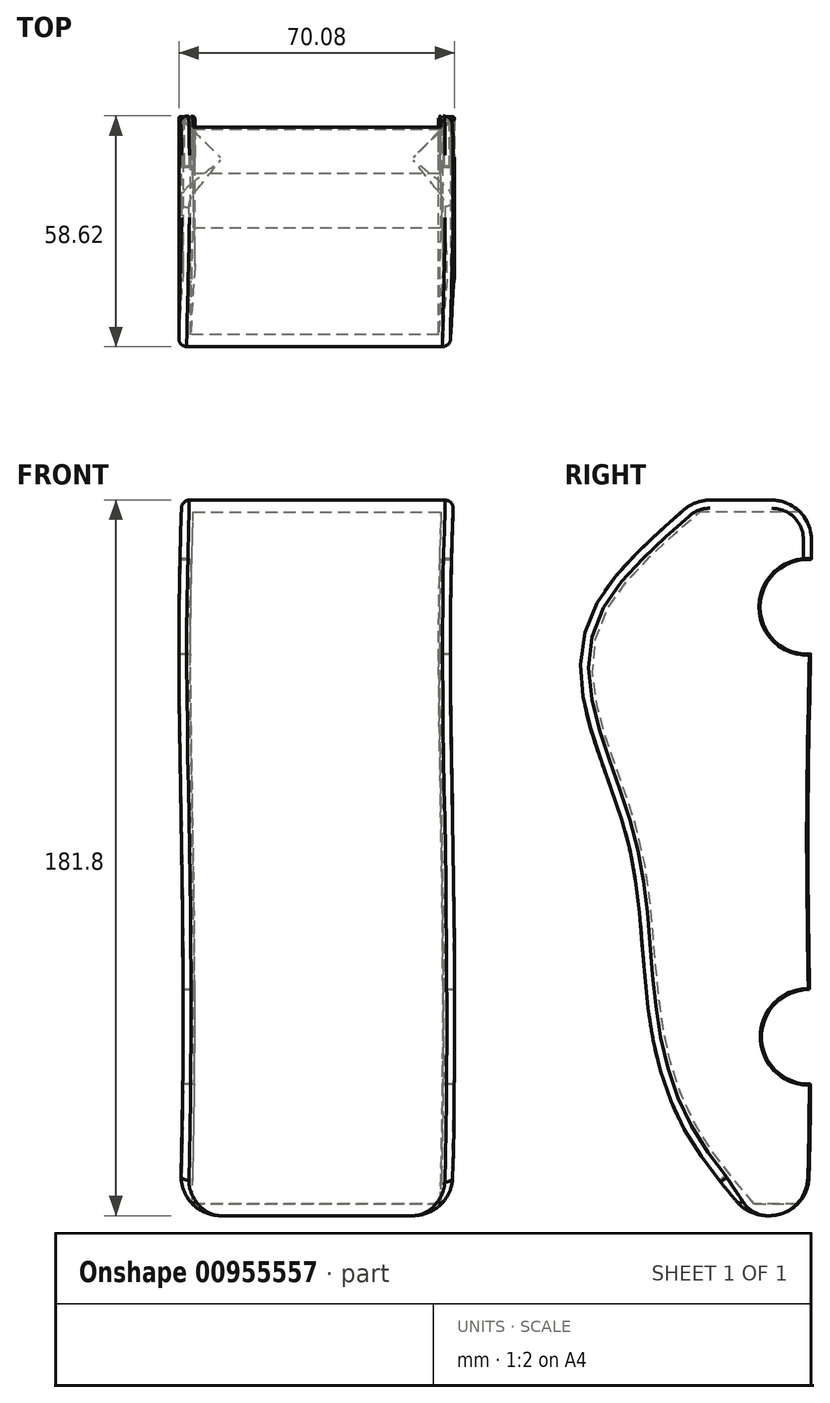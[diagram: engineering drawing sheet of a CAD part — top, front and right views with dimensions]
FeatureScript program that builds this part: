
annotation { "Feature Type Name" : "Feature", "Feature Type Description" : "" }
export const myFeature = defineFeature(function(context is Context, id is Id, definition is map)
    precondition{}
    {
        {
            var Q0;
            Q0=qCreatedBy(makeId("Top.planeOp"),FACE);
            var sketch = newSketch(context, id + "F0", { "sketchPlane" : qUnion([Q0])});
            skLineSegment(sketch, "E0.bottom", {"start": v(34.5, -14.38) * mm, "end": v(-34.5, -14.38) * mm});
            skLineSegment(sketch, "E0.top", {"start": v(34.5, 14.38) * mm, "end": v(-34.5, 14.38) * mm});
            skLineSegment(sketch, "E0.left", {"start": v(34.5, -14.38) * mm, "end": v(34.5, 14.38) * mm});
            skLineSegment(sketch, "E0.right", {"start": v(-34.5, -14.38) * mm, "end": v(-34.5, 14.38) * mm});
            skPoint(sketch, "E0.middle", {"position": v(0, 0) * mm});
            skSolve(sketch);
        }
        {
            var Q0;
            Q0=qCreatedBy(makeId("Top.planeOp"),FACE);
            cPlane(context, id + "F1", {"entities" : qUnion([Q0]), "cplaneType" : CPlaneType.OFFSET, "offset" : 80 * mm, "width" : 150 * mm, "height" : 150 * mm});
        }
        {
            var Q0;
            Q0=qCreatedBy(id+"F1.planeOp",FACE);
            var sketch = newSketch(context, id + "F2", { "sketchPlane" : qUnion([Q0])});
            skLineSegment(sketch, "E1.bottom", {"start": v(-34.6, 13.88) * mm, "end": v(34.4, 13.88) * mm});
            skLineSegment(sketch, "E1.top", {"start": v(-34.6, -32.29) * mm, "end": v(34.4, -32.29) * mm});
            skLineSegment(sketch, "E1.left", {"start": v(-34.6, 13.88) * mm, "end": v(-34.6, -32.29) * mm});
            skLineSegment(sketch, "E1.right", {"start": v(34.4, 13.88) * mm, "end": v(34.4, -32.29) * mm});
            skSolve(sketch);
        }
        {
            var Q0;
            Q0=qCreatedBy(id+"F1.planeOp",FACE);
            cPlane(context, id + "F3", {"entities" : qUnion([Q0]), "cplaneType" : CPlaneType.OFFSET, "offset" : 60 * mm, "width" : 150 * mm, "height" : 150 * mm});
        }
        {
            var Q0;
            Q0=qCreatedBy(id+"F3.planeOp",FACE);
            var sketch = newSketch(context, id + "F4", { "sketchPlane" : qUnion([Q0])});
            skLineSegment(sketch, "E2.bottom", {"start": v(-35.14, 14.76) * mm, "end": v(33.86, 14.76) * mm});
            skLineSegment(sketch, "E2.top", {"start": v(-35.14, -39) * mm, "end": v(33.86, -39) * mm});
            skLineSegment(sketch, "E2.left", {"start": v(-35.14, 14.76) * mm, "end": v(-35.14, -39) * mm});
            skLineSegment(sketch, "E2.right", {"start": v(33.86, 14.76) * mm, "end": v(33.86, -39) * mm});
            skSolve(sketch);
        }
        {
            var Q0;
            Q0=makeQuery(id+"F4.imprint","IMPRINT",FACE,{"disambiguationData":[TD([[makeQuery(id+"F4.imprint","IMPRINT",EDGE,{"derivedFrom":sQuery(id+"F4.wireOp",EDGE,"E2.bottom")}),-1.0]])]});
            cPlane(context, id + "F5", {"entities" : qUnion([Q0]), "cplaneType" : CPlaneType.OFFSET, "offset" : 25 * mm, "width" : 150 * mm, "height" : 150 * mm});
        }
        {
            var Q0;
            Q0=qCreatedBy(id+"F5.planeOp",FACE);
            var sketch = newSketch(context, id + "F6", { "sketchPlane" : qUnion([Q0])});
            skLineSegment(sketch, "E3.bottom", {"start": v(-34.5, -14.73) * mm, "end": v(34.5, -14.73) * mm});
            skLineSegment(sketch, "E3.top", {"start": v(-34.5, 14.73) * mm, "end": v(34.5, 14.73) * mm});
            skLineSegment(sketch, "E3.left", {"start": v(-34.5, -14.73) * mm, "end": v(-34.5, 14.73) * mm});
            skLineSegment(sketch, "E3.right", {"start": v(34.5, -14.73) * mm, "end": v(34.5, 14.73) * mm});
            skPoint(sketch, "E3.middle", {"position": v(0, 0) * mm});
            skSolve(sketch);
        }
        {
            var Q0;
            Q0=qCreatedBy(makeId("Right.planeOp"),FACE);
            var sketch = newSketch(context, id + "F7", { "sketchPlane" : qUnion([Q0])});
            skCircle(sketch, "E4", {"center": v(13.75, 137.88) * mm, "radius": 12 * mm});
            skCircle(sketch, "E5", {"center": v(14.12, 28.64) * mm, "radius": 12 * mm});
            skSolve(sketch);
        }
        {
            var Q0;
            Q0=makeQuery(id+"F0.imprint","IMPRINT",FACE,{"disambiguationData":[TD([[makeQuery(id+"F0.imprint","IMPRINT",EDGE,{"derivedFrom":sQuery(id+"F0.wireOp",EDGE,"E0.bottom")}),-1.0]])]});
            cPlane(context, id + "F8", {"entities" : qUnion([Q0]), "cplaneType" : CPlaneType.OFFSET, "offset" : 16.8 * mm, "oppositeDirection" : true, "width" : 150 * mm, "height" : 150 * mm});
        }
        {
            var Q0;
            Q0=qCreatedBy(id+"F8.planeOp",FACE);
            var sketch = newSketch(context, id + "F9", { "sketchPlane" : qUnion([Q0])});
            skLineSegment(sketch, "E6.bottom", {"start": v(-34.94, -1.1) * mm, "end": v(34.06, -1.1) * mm});
            skLineSegment(sketch, "E6.top", {"start": v(-34.94, 13.85) * mm, "end": v(34.06, 13.85) * mm});
            skLineSegment(sketch, "E6.left", {"start": v(-34.94, -1.1) * mm, "end": v(-34.94, 13.85) * mm});
            skLineSegment(sketch, "E6.right", {"start": v(34.06, -1.1) * mm, "end": v(34.06, 13.85) * mm});
            skSolve(sketch);
        }
        {
            var Q0;
            Q0=makeQuery(id+"F9.imprint","IMPRINT",FACE,{"disambiguationData":[TD([[makeQuery(id+"F9.imprint","IMPRINT",EDGE,{"derivedFrom":sQuery(id+"F9.wireOp",EDGE,"E6.bottom")}),1.0]])]});
            var Q1;
            Q1=makeQuery(id+"F0.imprint","IMPRINT",FACE,{"disambiguationData":[TD([[makeQuery(id+"F0.imprint","IMPRINT",EDGE,{"derivedFrom":sQuery(id+"F0.wireOp",EDGE,"E0.bottom")}),-1.0]])]});
            var Q2;
            Q2=makeQuery(id+"F2.imprint","IMPRINT",FACE,{"disambiguationData":[TD([[makeQuery(id+"F2.imprint","IMPRINT",EDGE,{"derivedFrom":sQuery(id+"F2.wireOp",EDGE,"E1.bottom")}),-1.0]])]});
            var Q3;
            Q3=makeQuery(id+"F4.imprint","IMPRINT",FACE,{"disambiguationData":[TD([[makeQuery(id+"F4.imprint","IMPRINT",EDGE,{"derivedFrom":sQuery(id+"F4.wireOp",EDGE,"E2.bottom")}),-1.0]])]});
            var Q4;
            Q4=makeQuery(id+"F6.imprint","IMPRINT",FACE,{"disambiguationData":[TD([[makeQuery(id+"F6.imprint","IMPRINT",EDGE,{"derivedFrom":sQuery(id+"F6.wireOp",EDGE,"E3.bottom")}),1.0]])]});
            loft(context, id + "F10", {"sheetProfilesArray" : [{ "sheetProfileEntities" : qUnion([Q0]) }, { "sheetProfileEntities" : qUnion([Q1]) }, { "sheetProfileEntities" : qUnion([Q2]) }, { "sheetProfileEntities" : qUnion([Q3]) }, { "sheetProfileEntities" : qUnion([Q4]) }]});
        }
        {
            var Q0;
            Q0=makeQuery(id+"F10.opLoft","SWEPT_FACE",FACE,{"disambiguationData":[OSD([sQuery(id+"F0.wireOp",EDGE,"E0.top"),sQuery(id+"F0.wireOp",EDGE,"E0.left"),sQuery(id+"F0.wireOp",EDGE,"E0.right"),sQuery(id+"F2.wireOp",EDGE,"E1.bottom"),sQuery(id+"F2.wireOp",EDGE,"E1.left"),sQuery(id+"F2.wireOp",EDGE,"E1.right"),sQuery(id+"F4.wireOp",EDGE,"E2.bottom"),sQuery(id+"F4.wireOp",EDGE,"E2.left"),sQuery(id+"F4.wireOp",EDGE,"E2.right"),sQuery(id+"F6.wireOp",EDGE,"E3.top"),sQuery(id+"F6.wireOp",EDGE,"E3.left"),sQuery(id+"F6.wireOp",EDGE,"E3.right"),sQuery(id+"F9.wireOp",EDGE,"E6.top"),sQuery(id+"F9.wireOp",EDGE,"E6.left"),sQuery(id+"F9.wireOp",EDGE,"E6.right")])]});
            shell(context, id + "F11", {"entities" : qUnion([Q0]), "thickness" : 3 * mm});
        }
        {
            var Q0;
            Q0=makeQuery(id+"F7.imprint","IMPRINT",FACE,{"disambiguationData":[TD([[makeQuery(id+"F7.imprint","IMPRINT",EDGE,{"derivedFrom":sQuery(id+"F7.wireOp",EDGE,"E5")}),1.0]])]});
            var Q1;
            Q1=makeQuery(id+"F7.imprint","IMPRINT",FACE,{"disambiguationData":[TD([[makeQuery(id+"F7.imprint","IMPRINT",EDGE,{"derivedFrom":sQuery(id+"F7.wireOp",EDGE,"E4")}),1.0]])]});
            extrude(context, id + "F12", {"entities" : qUnion([Q0, Q1]), "operationType" : NewBodyOperationType.REMOVE, "endBound" : BoundingType.SYMMETRIC, "oppositeDirection" : true, "depth" : 5000 * mm, "offsetDistance" : 25 * mm});
        }
        {
            var Q0;
            Q0=makeQuery(id+"F10.opLoft","CAP_FACE",FACE,{"disambiguationData":[OSD([makeQuery(id+"F9.imprint","IMPRINT",FACE,{"disambiguationData":[TD([[makeQuery(id+"F9.imprint","IMPRINT",EDGE,{"derivedFrom":sQuery(id+"F9.wireOp",EDGE,"E6.bottom")}),1.0]])]})])],"isStart":true});
            fillet(context, id + "F13", {"entities" : qUnion([Q0]), "radius" : 10 * mm, "tangentPropagation" : true, "allowEdgeOverflow" : false});
        }
        {
            var Q0;
            Q0=makeQuery(id+"F10.opLoft","MID_CAP_EDGE",EDGE,{"disambiguationData":[OSD([sQuery(id+"F6.wireOp",EDGE,"E3.top"),sQuery(id+"F6.wireOp",EDGE,"E3.left"),sQuery(id+"F6.wireOp",EDGE,"E3.right")])],"capPos":4.0});
            fillet(context, id + "F14", {"entities" : qUnion([Q0]), "radius" : 10 * mm, "tangentPropagation" : true, "allowEdgeOverflow" : false});
        }
        {
            var Q0;
            Q0=makeQuery(id+"F10.opLoft","MID_CAP_EDGE",EDGE,{"disambiguationData":[OSD([sQuery(id+"F6.wireOp",EDGE,"E3.bottom"),sQuery(id+"F6.wireOp",EDGE,"E3.left"),sQuery(id+"F6.wireOp",EDGE,"E3.right")])],"capPos":4.0});
            fillet(context, id + "F15", {"entities" : qUnion([Q0]), "radius" : 10 * mm, "tangentPropagation" : true, "allowEdgeOverflow" : false});
        }
        {
            var Q0;
            Q0=makeQuery(id+"F10.opLoft","SWEPT_EDGE",EDGE,{"disambiguationData":[OSD([sQuery(id+"F0.wireOp",EDGE,"E0.bottom"),sQuery(id+"F0.wireOp",EDGE,"E0.right"),sQuery(id+"F2.wireOp",EDGE,"E1.top"),sQuery(id+"F2.wireOp",EDGE,"E1.left"),sQuery(id+"F4.wireOp",EDGE,"E2.top"),sQuery(id+"F4.wireOp",EDGE,"E2.left"),sQuery(id+"F6.wireOp",EDGE,"E3.bottom"),sQuery(id+"F6.wireOp",EDGE,"E3.left"),sQuery(id+"F9.wireOp",EDGE,"E6.bottom"),sQuery(id+"F9.wireOp",EDGE,"E6.left")])]});
            var Q1;
            Q1=makeQuery(id+"F10.opLoft","SWEPT_EDGE",EDGE,{"disambiguationData":[OSD([sQuery(id+"F0.wireOp",EDGE,"E0.bottom"),sQuery(id+"F0.wireOp",EDGE,"E0.left"),sQuery(id+"F2.wireOp",EDGE,"E1.top"),sQuery(id+"F2.wireOp",EDGE,"E1.right"),sQuery(id+"F4.wireOp",EDGE,"E2.top"),sQuery(id+"F4.wireOp",EDGE,"E2.right"),sQuery(id+"F6.wireOp",EDGE,"E3.bottom"),sQuery(id+"F6.wireOp",EDGE,"E3.right"),sQuery(id+"F9.wireOp",EDGE,"E6.bottom"),sQuery(id+"F9.wireOp",EDGE,"E6.right")])]});
            fillet(context, id + "F16", {"entities" : qUnion([Q0, Q1]), "radius" : 2 * mm, "tangentPropagation" : true, "allowEdgeOverflow" : false});
        }
        {
            var Q0;
            {var subQ0=sQuery(id+"F9.wireOp",EDGE,"E6.left");var subQ1=sQuery(id+"F9.wireOp",EDGE,"E6.top");var subQ2=sQuery(id+"F6.wireOp",EDGE,"E3.left");var subQ3=sQuery(id+"F6.wireOp",EDGE,"E3.top");var subQ4=sQuery(id+"F4.wireOp",EDGE,"E2.left");var subQ5=sQuery(id+"F4.wireOp",EDGE,"E2.bottom");var subQ6=sQuery(id+"F2.wireOp",EDGE,"E1.left");var subQ7=sQuery(id+"F2.wireOp",EDGE,"E1.bottom");var subQ8=sQuery(id+"F0.wireOp",EDGE,"E0.right");var subQ9=sQuery(id+"F0.wireOp",EDGE,"E0.top");Q0=makeQuery(id+"F12.boolean.opBoolean","SPLIT",EDGE,{"disambiguationData":[TD([makeQuery(id+"F10.opLoft","SWEPT_FACE",FACE,{"disambiguationData":[OSD([sQuery(id+"F0.wireOp",EDGE,"E0.bottom"),subQ9,subQ8,subQ7,sQuery(id+"F2.wireOp",EDGE,"E1.top"),subQ6,subQ5,sQuery(id+"F4.wireOp",EDGE,"E2.top"),subQ4,sQuery(id+"F6.wireOp",EDGE,"E3.bottom"),subQ3,subQ2,sQuery(id+"F9.wireOp",EDGE,"E6.bottom"),subQ1,subQ0])]}),makeQuery(id+"F10.opLoft","SWEPT_FACE",FACE,{"disambiguationData":[OSD([subQ9,sQuery(id+"F0.wireOp",EDGE,"E0.left"),subQ8,subQ7,subQ6,sQuery(id+"F2.wireOp",EDGE,"E1.right"),subQ5,subQ4,sQuery(id+"F4.wireOp",EDGE,"E2.right"),subQ3,subQ2,sQuery(id+"F6.wireOp",EDGE,"E3.right"),subQ1,subQ0,sQuery(id+"F9.wireOp",EDGE,"E6.right")])]}),makeQuery(id+"F12.opExtrude","SWEPT_FACE",FACE,{"disambiguationData":[OSD([sQuery(id+"F7.wireOp",EDGE,"E4")])]}),makeQuery(id+"F12.opExtrude","SWEPT_FACE",FACE,{"disambiguationData":[OSD([sQuery(id+"F7.wireOp",EDGE,"E5")])]})])],"derivedFrom":makeQuery(id+"F10.opLoft","SWEPT_EDGE",EDGE,{"disambiguationData":[OSD([subQ9,subQ8,subQ7,subQ6,subQ5,subQ4,subQ3,subQ2,subQ1,subQ0])]})});}
            var Q1;
            Q1=makeQuery(id+"F12.boolean.opBoolean","INTERSECT",EDGE,{"derivedFrom":[makeQuery(id+"F10.opLoft","SWEPT_FACE",FACE,{"disambiguationData":[OSD([sQuery(id+"F0.wireOp",EDGE,"E0.bottom"),sQuery(id+"F0.wireOp",EDGE,"E0.top"),sQuery(id+"F0.wireOp",EDGE,"E0.right"),sQuery(id+"F2.wireOp",EDGE,"E1.bottom"),sQuery(id+"F2.wireOp",EDGE,"E1.top"),sQuery(id+"F2.wireOp",EDGE,"E1.left"),sQuery(id+"F4.wireOp",EDGE,"E2.bottom"),sQuery(id+"F4.wireOp",EDGE,"E2.top"),sQuery(id+"F4.wireOp",EDGE,"E2.left"),sQuery(id+"F6.wireOp",EDGE,"E3.bottom"),sQuery(id+"F6.wireOp",EDGE,"E3.top"),sQuery(id+"F6.wireOp",EDGE,"E3.left"),sQuery(id+"F9.wireOp",EDGE,"E6.bottom"),sQuery(id+"F9.wireOp",EDGE,"E6.top"),sQuery(id+"F9.wireOp",EDGE,"E6.left")])]}),makeQuery(id+"F12.opExtrude","SWEPT_FACE",FACE,{"disambiguationData":[OSD([sQuery(id+"F7.wireOp",EDGE,"E4")])]})]});
            var Q2;
            {var subQ0=sQuery(id+"F9.wireOp",EDGE,"E6.left");var subQ1=sQuery(id+"F9.wireOp",EDGE,"E6.top");var subQ2=sQuery(id+"F9.wireOp",EDGE,"E6.bottom");var subQ3=sQuery(id+"F6.wireOp",EDGE,"E3.left");var subQ4=sQuery(id+"F6.wireOp",EDGE,"E3.top");var subQ5=sQuery(id+"F4.wireOp",EDGE,"E2.left");var subQ6=sQuery(id+"F4.wireOp",EDGE,"E2.bottom");var subQ7=sQuery(id+"F2.wireOp",EDGE,"E1.left");var subQ8=sQuery(id+"F2.wireOp",EDGE,"E1.bottom");var subQ9=sQuery(id+"F0.wireOp",EDGE,"E0.right");var subQ10=sQuery(id+"F0.wireOp",EDGE,"E0.top");var subQ11=sQuery(id+"F9.wireOp",EDGE,"E6.right");Q2=makeQuery(id+"F12.boolean.opBoolean","SPLIT",EDGE,{"disambiguationData":[TD([makeQuery(id+"F10.opLoft","SWEPT_FACE",FACE,{"disambiguationData":[OSD([sQuery(id+"F0.wireOp",EDGE,"E0.bottom"),subQ10,subQ9,subQ8,sQuery(id+"F2.wireOp",EDGE,"E1.top"),subQ7,subQ6,sQuery(id+"F4.wireOp",EDGE,"E2.top"),subQ5,sQuery(id+"F6.wireOp",EDGE,"E3.bottom"),subQ4,subQ3,subQ2,subQ1,subQ0])]}),makeQuery(id+"F10.opLoft","SWEPT_FACE",FACE,{"disambiguationData":[OSD([subQ10,sQuery(id+"F0.wireOp",EDGE,"E0.left"),subQ9,subQ8,subQ7,sQuery(id+"F2.wireOp",EDGE,"E1.right"),subQ6,subQ5,sQuery(id+"F4.wireOp",EDGE,"E2.right"),subQ4,subQ3,sQuery(id+"F6.wireOp",EDGE,"E3.right"),subQ1,subQ0,subQ11])]}),makeQuery(id+"F10.opLoft","CAP_FACE",FACE,{"disambiguationData":[OSD([makeQuery(id+"F9.imprint","IMPRINT",FACE,{"disambiguationData":[TD([[makeQuery(id+"F9.imprint","IMPRINT",EDGE,{"derivedFrom":subQ2}),1.0]])]})])],"isStart":true}),makeQuery(id+"F12.opExtrude","SWEPT_FACE",FACE,{"disambiguationData":[OSD([sQuery(id+"F7.wireOp",EDGE,"E5")])]})])],"derivedFrom":makeQuery(id+"F10.opLoft","SWEPT_EDGE",EDGE,{"disambiguationData":[OSD([subQ10,subQ9,subQ8,subQ7,subQ6,subQ5,subQ4,subQ3,subQ1,subQ0])]})});}
            var Q3;
            Q3=makeQuery(id+"F12.boolean.opBoolean","INTERSECT",EDGE,{"derivedFrom":[makeQuery(id+"F10.opLoft","SWEPT_FACE",FACE,{"disambiguationData":[OSD([sQuery(id+"F0.wireOp",EDGE,"E0.bottom"),sQuery(id+"F0.wireOp",EDGE,"E0.top"),sQuery(id+"F0.wireOp",EDGE,"E0.right"),sQuery(id+"F2.wireOp",EDGE,"E1.bottom"),sQuery(id+"F2.wireOp",EDGE,"E1.top"),sQuery(id+"F2.wireOp",EDGE,"E1.left"),sQuery(id+"F4.wireOp",EDGE,"E2.bottom"),sQuery(id+"F4.wireOp",EDGE,"E2.top"),sQuery(id+"F4.wireOp",EDGE,"E2.left"),sQuery(id+"F6.wireOp",EDGE,"E3.bottom"),sQuery(id+"F6.wireOp",EDGE,"E3.top"),sQuery(id+"F6.wireOp",EDGE,"E3.left"),sQuery(id+"F9.wireOp",EDGE,"E6.bottom"),sQuery(id+"F9.wireOp",EDGE,"E6.top"),sQuery(id+"F9.wireOp",EDGE,"E6.left")])]}),makeQuery(id+"F12.opExtrude","SWEPT_FACE",FACE,{"disambiguationData":[OSD([sQuery(id+"F7.wireOp",EDGE,"E5")])]})]});
            var Q4;
            Q4=makeQuery(id+"F12.boolean.opBoolean","INTERSECT",EDGE,{"derivedFrom":[makeQuery(id+"F11.opShell","OFFSET_FACE",FACE,{"disambiguationData":[OSD([sQuery(id+"F0.wireOp",EDGE,"E0.bottom"),sQuery(id+"F0.wireOp",EDGE,"E0.top"),sQuery(id+"F0.wireOp",EDGE,"E0.right"),sQuery(id+"F2.wireOp",EDGE,"E1.bottom"),sQuery(id+"F2.wireOp",EDGE,"E1.top"),sQuery(id+"F2.wireOp",EDGE,"E1.left"),sQuery(id+"F4.wireOp",EDGE,"E2.bottom"),sQuery(id+"F4.wireOp",EDGE,"E2.top"),sQuery(id+"F4.wireOp",EDGE,"E2.left"),sQuery(id+"F6.wireOp",EDGE,"E3.bottom"),sQuery(id+"F6.wireOp",EDGE,"E3.top"),sQuery(id+"F6.wireOp",EDGE,"E3.left"),sQuery(id+"F9.wireOp",EDGE,"E6.bottom"),sQuery(id+"F9.wireOp",EDGE,"E6.top"),sQuery(id+"F9.wireOp",EDGE,"E6.left")])]}),makeQuery(id+"F12.opExtrude","SWEPT_FACE",FACE,{"disambiguationData":[OSD([sQuery(id+"F7.wireOp",EDGE,"E5")])]})]});
            var Q5;
            {var subQ0=sQuery(id+"F9.wireOp",EDGE,"E6.left");var subQ1=sQuery(id+"F9.wireOp",EDGE,"E6.top");var subQ2=sQuery(id+"F6.wireOp",EDGE,"E3.left");var subQ3=sQuery(id+"F6.wireOp",EDGE,"E3.top");var subQ4=sQuery(id+"F4.wireOp",EDGE,"E2.left");var subQ5=sQuery(id+"F4.wireOp",EDGE,"E2.bottom");var subQ6=sQuery(id+"F2.wireOp",EDGE,"E1.left");var subQ7=sQuery(id+"F2.wireOp",EDGE,"E1.bottom");var subQ8=sQuery(id+"F0.wireOp",EDGE,"E0.right");var subQ9=sQuery(id+"F0.wireOp",EDGE,"E0.top");Q5=makeQuery(id+"F12.boolean.opBoolean","SPLIT",EDGE,{"disambiguationData":[TD([makeQuery(id+"F10.opLoft","SWEPT_FACE",FACE,{"disambiguationData":[OSD([subQ9,sQuery(id+"F0.wireOp",EDGE,"E0.left"),subQ8,subQ7,subQ6,sQuery(id+"F2.wireOp",EDGE,"E1.right"),subQ5,subQ4,sQuery(id+"F4.wireOp",EDGE,"E2.right"),subQ3,subQ2,sQuery(id+"F6.wireOp",EDGE,"E3.right"),subQ1,subQ0,sQuery(id+"F9.wireOp",EDGE,"E6.right")])]}),makeQuery(id+"F11.opShell","OFFSET_FACE",FACE,{"disambiguationData":[OSD([sQuery(id+"F0.wireOp",EDGE,"E0.bottom"),subQ9,subQ8,subQ7,sQuery(id+"F2.wireOp",EDGE,"E1.top"),subQ6,subQ5,sQuery(id+"F4.wireOp",EDGE,"E2.top"),subQ4,sQuery(id+"F6.wireOp",EDGE,"E3.bottom"),subQ3,subQ2,sQuery(id+"F9.wireOp",EDGE,"E6.bottom"),subQ1,subQ0])]}),makeQuery(id+"F12.opExtrude","SWEPT_FACE",FACE,{"disambiguationData":[OSD([sQuery(id+"F7.wireOp",EDGE,"E4")])]}),makeQuery(id+"F12.opExtrude","SWEPT_FACE",FACE,{"disambiguationData":[OSD([sQuery(id+"F7.wireOp",EDGE,"E5")])]})])],"derivedFrom":makeQuery(id+"F11.opShell","OFFSET_EDGE",EDGE,{"disambiguationData":[OSD([subQ9,subQ8,subQ7,subQ6,subQ5,subQ4,subQ3,subQ2,subQ1,subQ0])]})});}
            var Q6;
            Q6=makeQuery(id+"F12.boolean.opBoolean","INTERSECT",EDGE,{"derivedFrom":[makeQuery(id+"F11.opShell","OFFSET_FACE",FACE,{"disambiguationData":[OSD([sQuery(id+"F0.wireOp",EDGE,"E0.bottom"),sQuery(id+"F0.wireOp",EDGE,"E0.top"),sQuery(id+"F0.wireOp",EDGE,"E0.right"),sQuery(id+"F2.wireOp",EDGE,"E1.bottom"),sQuery(id+"F2.wireOp",EDGE,"E1.top"),sQuery(id+"F2.wireOp",EDGE,"E1.left"),sQuery(id+"F4.wireOp",EDGE,"E2.bottom"),sQuery(id+"F4.wireOp",EDGE,"E2.top"),sQuery(id+"F4.wireOp",EDGE,"E2.left"),sQuery(id+"F6.wireOp",EDGE,"E3.bottom"),sQuery(id+"F6.wireOp",EDGE,"E3.top"),sQuery(id+"F6.wireOp",EDGE,"E3.left"),sQuery(id+"F9.wireOp",EDGE,"E6.bottom"),sQuery(id+"F9.wireOp",EDGE,"E6.top"),sQuery(id+"F9.wireOp",EDGE,"E6.left")])]}),makeQuery(id+"F12.opExtrude","SWEPT_FACE",FACE,{"disambiguationData":[OSD([sQuery(id+"F7.wireOp",EDGE,"E4")])]})]});
            var Q7;
            {var subQ0=sQuery(id+"F9.wireOp",EDGE,"E6.right");var subQ1=sQuery(id+"F9.wireOp",EDGE,"E6.top");var subQ2=sQuery(id+"F6.wireOp",EDGE,"E3.right");var subQ3=sQuery(id+"F6.wireOp",EDGE,"E3.top");var subQ4=sQuery(id+"F4.wireOp",EDGE,"E2.right");var subQ5=sQuery(id+"F4.wireOp",EDGE,"E2.bottom");var subQ6=sQuery(id+"F2.wireOp",EDGE,"E1.right");var subQ7=sQuery(id+"F2.wireOp",EDGE,"E1.bottom");var subQ8=sQuery(id+"F0.wireOp",EDGE,"E0.left");var subQ9=sQuery(id+"F0.wireOp",EDGE,"E0.top");Q7=makeQuery(id+"F12.boolean.opBoolean","SPLIT",EDGE,{"disambiguationData":[TD([makeQuery(id+"F10.opLoft","SWEPT_FACE",FACE,{"disambiguationData":[OSD([sQuery(id+"F0.wireOp",EDGE,"E0.bottom"),subQ9,subQ8,subQ7,sQuery(id+"F2.wireOp",EDGE,"E1.top"),subQ6,subQ5,sQuery(id+"F4.wireOp",EDGE,"E2.top"),subQ4,sQuery(id+"F6.wireOp",EDGE,"E3.bottom"),subQ3,subQ2,sQuery(id+"F9.wireOp",EDGE,"E6.bottom"),subQ1,subQ0])]}),makeQuery(id+"F10.opLoft","SWEPT_FACE",FACE,{"disambiguationData":[OSD([subQ9,subQ8,sQuery(id+"F0.wireOp",EDGE,"E0.right"),subQ7,sQuery(id+"F2.wireOp",EDGE,"E1.left"),subQ6,subQ5,sQuery(id+"F4.wireOp",EDGE,"E2.left"),subQ4,subQ3,sQuery(id+"F6.wireOp",EDGE,"E3.left"),subQ2,subQ1,sQuery(id+"F9.wireOp",EDGE,"E6.left"),subQ0])]}),makeQuery(id+"F12.opExtrude","SWEPT_FACE",FACE,{"disambiguationData":[OSD([sQuery(id+"F7.wireOp",EDGE,"E4")])]}),makeQuery(id+"F12.opExtrude","SWEPT_FACE",FACE,{"disambiguationData":[OSD([sQuery(id+"F7.wireOp",EDGE,"E5")])]})])],"derivedFrom":makeQuery(id+"F10.opLoft","SWEPT_EDGE",EDGE,{"disambiguationData":[OSD([subQ9,subQ8,subQ7,subQ6,subQ5,subQ4,subQ3,subQ2,subQ1,subQ0])]})});}
            var Q8;
            {var subQ0=sQuery(id+"F9.wireOp",EDGE,"E6.right");var subQ1=sQuery(id+"F9.wireOp",EDGE,"E6.top");var subQ2=sQuery(id+"F6.wireOp",EDGE,"E3.right");var subQ3=sQuery(id+"F6.wireOp",EDGE,"E3.top");var subQ4=sQuery(id+"F4.wireOp",EDGE,"E2.right");var subQ5=sQuery(id+"F4.wireOp",EDGE,"E2.bottom");var subQ6=sQuery(id+"F2.wireOp",EDGE,"E1.right");var subQ7=sQuery(id+"F2.wireOp",EDGE,"E1.bottom");var subQ8=sQuery(id+"F0.wireOp",EDGE,"E0.left");var subQ9=sQuery(id+"F0.wireOp",EDGE,"E0.top");Q8=makeQuery(id+"F12.boolean.opBoolean","SPLIT",EDGE,{"disambiguationData":[TD([makeQuery(id+"F10.opLoft","SWEPT_FACE",FACE,{"disambiguationData":[OSD([subQ9,subQ8,sQuery(id+"F0.wireOp",EDGE,"E0.right"),subQ7,sQuery(id+"F2.wireOp",EDGE,"E1.left"),subQ6,subQ5,sQuery(id+"F4.wireOp",EDGE,"E2.left"),subQ4,subQ3,sQuery(id+"F6.wireOp",EDGE,"E3.left"),subQ2,subQ1,sQuery(id+"F9.wireOp",EDGE,"E6.left"),subQ0])]}),makeQuery(id+"F11.opShell","OFFSET_FACE",FACE,{"disambiguationData":[OSD([sQuery(id+"F0.wireOp",EDGE,"E0.bottom"),subQ9,subQ8,subQ7,sQuery(id+"F2.wireOp",EDGE,"E1.top"),subQ6,subQ5,sQuery(id+"F4.wireOp",EDGE,"E2.top"),subQ4,sQuery(id+"F6.wireOp",EDGE,"E3.bottom"),subQ3,subQ2,sQuery(id+"F9.wireOp",EDGE,"E6.bottom"),subQ1,subQ0])]}),makeQuery(id+"F12.opExtrude","SWEPT_FACE",FACE,{"disambiguationData":[OSD([sQuery(id+"F7.wireOp",EDGE,"E4")])]}),makeQuery(id+"F12.opExtrude","SWEPT_FACE",FACE,{"disambiguationData":[OSD([sQuery(id+"F7.wireOp",EDGE,"E5")])]})])],"derivedFrom":makeQuery(id+"F11.opShell","OFFSET_EDGE",EDGE,{"disambiguationData":[OSD([subQ9,subQ8,subQ7,subQ6,subQ5,subQ4,subQ3,subQ2,subQ1,subQ0])]})});}
            var Q9;
            Q9=makeQuery(id+"F12.boolean.opBoolean","INTERSECT",EDGE,{"derivedFrom":[makeQuery(id+"F10.opLoft","SWEPT_FACE",FACE,{"disambiguationData":[OSD([sQuery(id+"F0.wireOp",EDGE,"E0.bottom"),sQuery(id+"F0.wireOp",EDGE,"E0.top"),sQuery(id+"F0.wireOp",EDGE,"E0.left"),sQuery(id+"F2.wireOp",EDGE,"E1.bottom"),sQuery(id+"F2.wireOp",EDGE,"E1.top"),sQuery(id+"F2.wireOp",EDGE,"E1.right"),sQuery(id+"F4.wireOp",EDGE,"E2.bottom"),sQuery(id+"F4.wireOp",EDGE,"E2.top"),sQuery(id+"F4.wireOp",EDGE,"E2.right"),sQuery(id+"F6.wireOp",EDGE,"E3.bottom"),sQuery(id+"F6.wireOp",EDGE,"E3.top"),sQuery(id+"F6.wireOp",EDGE,"E3.right"),sQuery(id+"F9.wireOp",EDGE,"E6.bottom"),sQuery(id+"F9.wireOp",EDGE,"E6.top"),sQuery(id+"F9.wireOp",EDGE,"E6.right")])]}),makeQuery(id+"F12.opExtrude","SWEPT_FACE",FACE,{"disambiguationData":[OSD([sQuery(id+"F7.wireOp",EDGE,"E4")])]})]});
            var Q10;
            Q10=makeQuery(id+"F12.boolean.opBoolean","INTERSECT",EDGE,{"derivedFrom":[makeQuery(id+"F11.opShell","OFFSET_FACE",FACE,{"disambiguationData":[OSD([sQuery(id+"F0.wireOp",EDGE,"E0.bottom"),sQuery(id+"F0.wireOp",EDGE,"E0.top"),sQuery(id+"F0.wireOp",EDGE,"E0.left"),sQuery(id+"F2.wireOp",EDGE,"E1.bottom"),sQuery(id+"F2.wireOp",EDGE,"E1.top"),sQuery(id+"F2.wireOp",EDGE,"E1.right"),sQuery(id+"F4.wireOp",EDGE,"E2.bottom"),sQuery(id+"F4.wireOp",EDGE,"E2.top"),sQuery(id+"F4.wireOp",EDGE,"E2.right"),sQuery(id+"F6.wireOp",EDGE,"E3.bottom"),sQuery(id+"F6.wireOp",EDGE,"E3.top"),sQuery(id+"F6.wireOp",EDGE,"E3.right"),sQuery(id+"F9.wireOp",EDGE,"E6.bottom"),sQuery(id+"F9.wireOp",EDGE,"E6.top"),sQuery(id+"F9.wireOp",EDGE,"E6.right")])]}),makeQuery(id+"F12.opExtrude","SWEPT_FACE",FACE,{"disambiguationData":[OSD([sQuery(id+"F7.wireOp",EDGE,"E4")])]})]});
            var Q11;
            Q11=makeQuery(id+"F12.boolean.opBoolean","INTERSECT",EDGE,{"derivedFrom":[makeQuery(id+"F10.opLoft","SWEPT_FACE",FACE,{"disambiguationData":[OSD([sQuery(id+"F0.wireOp",EDGE,"E0.bottom"),sQuery(id+"F0.wireOp",EDGE,"E0.top"),sQuery(id+"F0.wireOp",EDGE,"E0.left"),sQuery(id+"F2.wireOp",EDGE,"E1.bottom"),sQuery(id+"F2.wireOp",EDGE,"E1.top"),sQuery(id+"F2.wireOp",EDGE,"E1.right"),sQuery(id+"F4.wireOp",EDGE,"E2.bottom"),sQuery(id+"F4.wireOp",EDGE,"E2.top"),sQuery(id+"F4.wireOp",EDGE,"E2.right"),sQuery(id+"F6.wireOp",EDGE,"E3.bottom"),sQuery(id+"F6.wireOp",EDGE,"E3.top"),sQuery(id+"F6.wireOp",EDGE,"E3.right"),sQuery(id+"F9.wireOp",EDGE,"E6.bottom"),sQuery(id+"F9.wireOp",EDGE,"E6.top"),sQuery(id+"F9.wireOp",EDGE,"E6.right")])]}),makeQuery(id+"F12.opExtrude","SWEPT_FACE",FACE,{"disambiguationData":[OSD([sQuery(id+"F7.wireOp",EDGE,"E5")])]})]});
            var Q12;
            Q12=makeQuery(id+"F12.boolean.opBoolean","INTERSECT",EDGE,{"derivedFrom":[makeQuery(id+"F11.opShell","OFFSET_FACE",FACE,{"disambiguationData":[OSD([sQuery(id+"F0.wireOp",EDGE,"E0.bottom"),sQuery(id+"F0.wireOp",EDGE,"E0.top"),sQuery(id+"F0.wireOp",EDGE,"E0.left"),sQuery(id+"F2.wireOp",EDGE,"E1.bottom"),sQuery(id+"F2.wireOp",EDGE,"E1.top"),sQuery(id+"F2.wireOp",EDGE,"E1.right"),sQuery(id+"F4.wireOp",EDGE,"E2.bottom"),sQuery(id+"F4.wireOp",EDGE,"E2.top"),sQuery(id+"F4.wireOp",EDGE,"E2.right"),sQuery(id+"F6.wireOp",EDGE,"E3.bottom"),sQuery(id+"F6.wireOp",EDGE,"E3.top"),sQuery(id+"F6.wireOp",EDGE,"E3.right"),sQuery(id+"F9.wireOp",EDGE,"E6.bottom"),sQuery(id+"F9.wireOp",EDGE,"E6.top"),sQuery(id+"F9.wireOp",EDGE,"E6.right")])]}),makeQuery(id+"F12.opExtrude","SWEPT_FACE",FACE,{"disambiguationData":[OSD([sQuery(id+"F7.wireOp",EDGE,"E5")])]})]});
            var Q13;
            {var subQ0=sQuery(id+"F9.wireOp",EDGE,"E6.right");var subQ1=sQuery(id+"F9.wireOp",EDGE,"E6.top");var subQ2=sQuery(id+"F9.wireOp",EDGE,"E6.bottom");var subQ3=sQuery(id+"F6.wireOp",EDGE,"E3.right");var subQ4=sQuery(id+"F6.wireOp",EDGE,"E3.top");var subQ5=sQuery(id+"F4.wireOp",EDGE,"E2.right");var subQ6=sQuery(id+"F4.wireOp",EDGE,"E2.bottom");var subQ7=sQuery(id+"F2.wireOp",EDGE,"E1.right");var subQ8=sQuery(id+"F2.wireOp",EDGE,"E1.bottom");var subQ9=sQuery(id+"F0.wireOp",EDGE,"E0.left");var subQ10=sQuery(id+"F0.wireOp",EDGE,"E0.top");var subQ11=sQuery(id+"F9.wireOp",EDGE,"E6.left");Q13=makeQuery(id+"F12.boolean.opBoolean","SPLIT",EDGE,{"disambiguationData":[TD([makeQuery(id+"F10.opLoft","SWEPT_FACE",FACE,{"disambiguationData":[OSD([sQuery(id+"F0.wireOp",EDGE,"E0.bottom"),subQ10,subQ9,subQ8,sQuery(id+"F2.wireOp",EDGE,"E1.top"),subQ7,subQ6,sQuery(id+"F4.wireOp",EDGE,"E2.top"),subQ5,sQuery(id+"F6.wireOp",EDGE,"E3.bottom"),subQ4,subQ3,subQ2,subQ1,subQ0])]}),makeQuery(id+"F10.opLoft","SWEPT_FACE",FACE,{"disambiguationData":[OSD([subQ10,subQ9,sQuery(id+"F0.wireOp",EDGE,"E0.right"),subQ8,sQuery(id+"F2.wireOp",EDGE,"E1.left"),subQ7,subQ6,sQuery(id+"F4.wireOp",EDGE,"E2.left"),subQ5,subQ4,sQuery(id+"F6.wireOp",EDGE,"E3.left"),subQ3,subQ1,subQ11,subQ0])]}),makeQuery(id+"F10.opLoft","CAP_FACE",FACE,{"disambiguationData":[OSD([makeQuery(id+"F9.imprint","IMPRINT",FACE,{"disambiguationData":[TD([[makeQuery(id+"F9.imprint","IMPRINT",EDGE,{"derivedFrom":subQ2}),1.0]])]})])],"isStart":true}),makeQuery(id+"F12.opExtrude","SWEPT_FACE",FACE,{"disambiguationData":[OSD([sQuery(id+"F7.wireOp",EDGE,"E5")])]})])],"derivedFrom":makeQuery(id+"F10.opLoft","SWEPT_EDGE",EDGE,{"disambiguationData":[OSD([subQ10,subQ9,subQ8,subQ7,subQ6,subQ5,subQ4,subQ3,subQ1,subQ0])]})});}
            var Q14;
            {var subQ0=sQuery(id+"F9.wireOp",EDGE,"E6.right");var subQ1=sQuery(id+"F9.wireOp",EDGE,"E6.left");var subQ2=sQuery(id+"F9.wireOp",EDGE,"E6.top");var subQ3=sQuery(id+"F6.wireOp",EDGE,"E3.right");var subQ4=sQuery(id+"F6.wireOp",EDGE,"E3.top");var subQ5=sQuery(id+"F4.wireOp",EDGE,"E2.right");var subQ6=sQuery(id+"F4.wireOp",EDGE,"E2.bottom");var subQ7=sQuery(id+"F2.wireOp",EDGE,"E1.right");var subQ8=sQuery(id+"F2.wireOp",EDGE,"E1.bottom");var subQ9=sQuery(id+"F0.wireOp",EDGE,"E0.left");var subQ10=sQuery(id+"F0.wireOp",EDGE,"E0.top");var subQ11=sQuery(id+"F9.wireOp",EDGE,"E6.bottom");Q14=makeQuery(id+"F12.boolean.opBoolean","SPLIT",EDGE,{"disambiguationData":[TD([makeQuery(id+"F10.opLoft","SWEPT_FACE",FACE,{"disambiguationData":[OSD([subQ10,subQ9,sQuery(id+"F0.wireOp",EDGE,"E0.right"),subQ8,sQuery(id+"F2.wireOp",EDGE,"E1.left"),subQ7,subQ6,sQuery(id+"F4.wireOp",EDGE,"E2.left"),subQ5,subQ4,sQuery(id+"F6.wireOp",EDGE,"E3.left"),subQ3,subQ2,subQ1,subQ0])]}),makeQuery(id+"F11.opShell","OFFSET_FACE",FACE,{"disambiguationData":[OSD([sQuery(id+"F0.wireOp",EDGE,"E0.bottom"),subQ10,subQ9,subQ8,sQuery(id+"F2.wireOp",EDGE,"E1.top"),subQ7,subQ6,sQuery(id+"F4.wireOp",EDGE,"E2.top"),subQ5,sQuery(id+"F6.wireOp",EDGE,"E3.bottom"),subQ4,subQ3,subQ11,subQ2,subQ0])]}),makeQuery(id+"F11.opShell","OFFSET_FACE",FACE,{"disambiguationData":[OSD([makeQuery(id+"F9.imprint","IMPRINT",FACE,{"disambiguationData":[TD([[makeQuery(id+"F9.imprint","IMPRINT",EDGE,{"derivedFrom":subQ11}),1.0]])]})])]}),makeQuery(id+"F12.opExtrude","SWEPT_FACE",FACE,{"disambiguationData":[OSD([sQuery(id+"F7.wireOp",EDGE,"E5")])]})])],"derivedFrom":makeQuery(id+"F11.opShell","OFFSET_EDGE",EDGE,{"disambiguationData":[OSD([subQ10,subQ9,subQ8,subQ7,subQ6,subQ5,subQ4,subQ3,subQ2,subQ0])]})});}
            fillet(context, id + "F17", {"entities" : qUnion([Q0, Q1, Q2, Q3, Q4, Q5, Q6, Q7, Q8, Q9, Q10, Q11, Q12, Q13, Q14]), "radius" : 0.3 * mm, "tangentPropagation" : true, "allowEdgeOverflow" : false});
        }
    });
